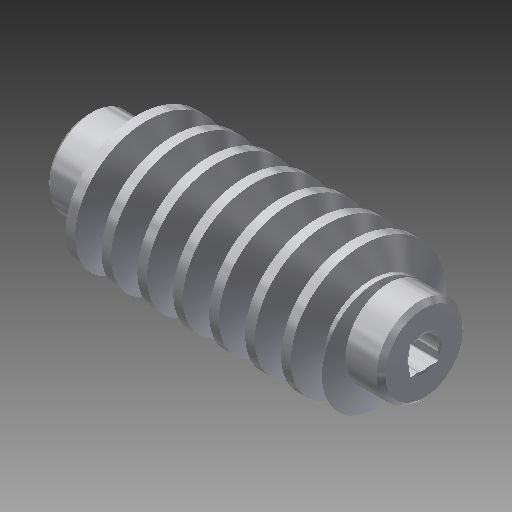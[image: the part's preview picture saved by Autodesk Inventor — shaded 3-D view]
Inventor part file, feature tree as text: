
AUTODESK INVENTOR PART (.ipt)
format: ipt  version: 2019 (Build 230136000, 136)  size: 440,832 bytes
history: native  units: mm (DEFAULTED — no unit token found)
features: other x5, extrude x4, sketch x4, chamfer x3, pattern_circular x2, revolve x1, mirror x1, fillet x1, projected_geometry x1
ambient origin geometry x6: Origin, XZ Plane, X Axis, Y Axis, Z Axis, Center Point
bodies: Solid1 (feature_tree)
feature tree (22):
  extrude  "Base Body"  Depth=15.523337mm
  chamfer  "Chamfer1"  Distance=2.845945mm
  chamfer  "Chamfer2"  Distance=1.035839mm
  other  "Tooth Sketch"
  other  "Tooth"
  pattern_circular  "Tooth Pattern"  [2 undecoded]
  other  "Left Tooth"
  pattern_circular  "Left Tooth Pattern"  [2 undecoded]
  extrude  "Extrusion2"  Depth=0.2mm
  chamfer  "Chamfer3"  Distance=19.198622mm
  revolve  "Revolution1"  [1 undecoded]
  mirror  "Mirror1"
  extrude  "Extrusion3"  Depth=0.2mm
  fillet  "Fillet1"  Radius=4.915723mm
  other  "Base Body Sketch"
  sketch  "Sketch5"  dims[d4=40.0mm d5=15.523337mm]
  other  "Srf1"
  sketch  "Sketch6"  dims[d6=30.0mm]
  sketch  "Sketch7"  dims[d7=0.0mm]
  sketch  "Sketch8"  dims[d8=1.035839mm d9=2.845945mm d10=1.035839mm d11=2.845945mm d12=19.198622mm d14=3.1425mm d24=19.198622mm d25=18.288mm d26=1.016mm d27=4.915723mm d28=6.468057mm d29=7.839285mm d30=4.064mm d31=10.0mm d32=100.0mm d33=0.0mm d34=90.0deg d35=90.0deg d36=0.0mm d37=0.0mm d44=10.0mm d46=360.0deg d47=45.0deg d48=45.0deg d49=20.0mm d50=0.0mm d54=0.0mm d56=0.0mm d59=13.0mm d60=10.0mm d61=0.0mm d62=4.064mm d63=10.0mm d64=100.0mm d65=0.0mm d66=90.0deg d67=90.0deg d68=0.0mm d69=0.0mm d70=10.0mm d71=10.0mm d72=10.0mm d73=360.0deg d75=10.0mm d76=10.0mm d77=0.0mm d79=20.0mm d80=0.0mm d81=4.0mm d82=0.0mm d83=0.05mm d84=0.5mm d85=2.0mm d86=45.0deg d87=8.0mm d88=16.5mm d89=90.0deg d90=3.25mm d91=3.25mm d92=1.625mm d93=1.625mm d94=10.0mm d95=0.0mm d96=3.5mm d97=0.2mm]
  extrude  "ExtrusionSrf1"  Depth=0.2mm
  projected_geometry  "Project Cut Edges1"
note: 5 required parameter values undecoded (feature->parameter linkage not recoverable at this tier; creation-order binding heuristic only, values carry confidence <= 0.55)